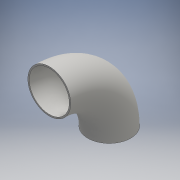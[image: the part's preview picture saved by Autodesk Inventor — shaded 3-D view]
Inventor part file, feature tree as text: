
AUTODESK INVENTOR PART (.ipt)
format: ipt  version: 2016 (Build 200138000, 138)  size: 152,576 bytes
history: native  units: mm
features: sweep x1, sketch x1
ambient origin geometry x8: Origin, YZ Plane, XZ Plane, XY Plane, X Axis, Y Axis, Z Axis, Center Point
bodies: Body1 (feature_tree)
feature tree (2):
  sweep  "Sweep2"
  sketch  "Sketch3"  dims[d14=273.0mm d15=9.27mm d16=0.0mm d17=0.0mm]
